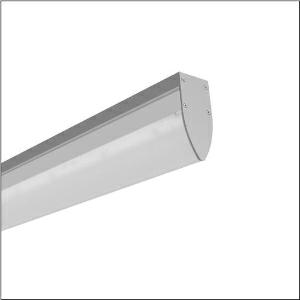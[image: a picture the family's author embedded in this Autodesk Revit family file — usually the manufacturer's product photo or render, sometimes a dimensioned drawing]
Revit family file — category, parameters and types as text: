
# Revit family: mira_21_td_51fr527g434a
name_source: partatom
category: Lighting Fixtures
units: mm (PartAtom-declared; Revit-internal decimal feet)

## family parameters
Cut with Voids When Loaded = No
Host = Face
Light Source = No
Part Type = Normal
Room Calculation Point = No
Round Connector Dimension = Use Diameter
Shared = No

## types (1)
- Mira 21 TD (1 x LED, 3020 lm, 20 W, 4000K)
    Apparent Load = 20 VA
    CIE Flux Codes = 40 68 87 81 100
    Color Rendering = 80
    Color Temperature = 4000K
    Default Elevation = 1800 mm
    Description = Mira 21 TD, clean room luminaire, primary light control with reflector, primary optical cover: cover, of PMMA, frosted, light emission: direct distribution, primary light characteristic: symmetric, installation type: surface-mounted, LED, rated luminous flux: 3.020lm, luminous efficacy: 151lm/W, light colour: 840, colour temperature: 4000K, control gear: ON/OFF, with terminal, 3-pole, max. 2.5mm², mains connection: 230V, AC, 50/60Hz, rated input power: 20W, luminaire housing, of sheet steel, coated, pure white (RAL 9010), length: 900mm, width: 55mm, height: 120mm, protection rating (complete): IP43, insulation class (complete): insulation class I (protective earthing), certification: CE, UKCA, permissible operating ambient temperature: -5..+40°C, standard: EN 50419, packaging unit: 1 piece
    Height = 120 mm
    Lamp = 1 x LED
    Lamp Light Flux = 3020 lm
    Lamp Power = 20 W
    Lamp count = 1
    Length = 900 mm
    Luminous efficacy = 151 lm/W
    Manufacturer = Siteco
    ModVariant = No
    Model = 51FR527G434A
    Mounting Place = Ceiling
    Mounting Type = Surface mounted
    Number of Poles = 1
    OnlyDefault = Yes
    Power Factor = 1
    Product Name = Mira 21 TD
    Product group = clean room luminaire | ceiling mounted
    ProductGroupID = 306
    Protection Class = Protection class I
    Protection Degree = IP 43
    RLX_Detail_Level = 1
    RLX_Emergency_Light_Flux = 0 lm
    RLX_Emergency_Type = 0
    RLX_Emergency_Type_DB = No
    RlxData = <blob elided: 25141 chars, md5=11770462>
    Socket = socket
    Standby Power = 0 W
    System Light Flux = 3020 lm
    System Power = 20 W
    Type Comments = Product without accessories
    Type Image = l_1007115.jpg
    URL = http://relux.com
    VarID = ---
    Voltage = 0 V
    Weight = 0.00 kg
    Width = 55 mm

## geometry (parser evidence)
native form markers: Blend x4, Sweep x14
no freeform markers — native parametric forms only
